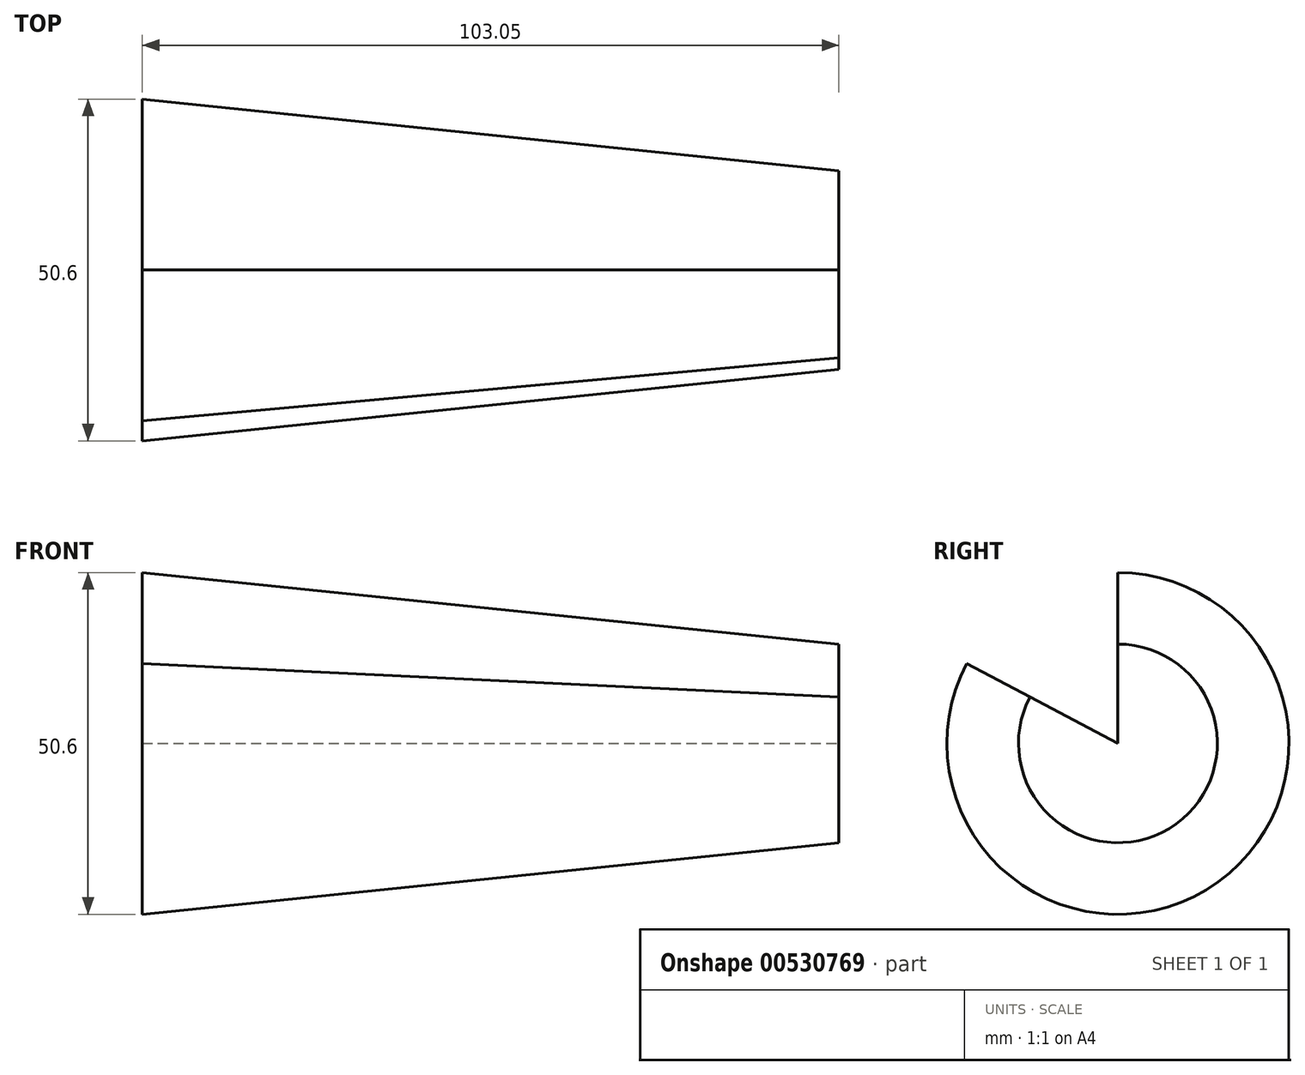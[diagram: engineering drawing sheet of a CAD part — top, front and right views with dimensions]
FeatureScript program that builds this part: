
annotation { "Feature Type Name" : "Feature", "Feature Type Description" : "" }
export const myFeature = defineFeature(function(context is Context, id is Id, definition is map)
    precondition{}
    {
        {
            var Q0;
            Q0=qCreatedBy(makeId("Front.planeOp"),FACE);
            var sketch = newSketch(context, id + "F0", { "sketchPlane" : qUnion([Q0])});
            skLineSegment(sketch, "E0.bottom", {"start": v(0, 0) * mm, "end": v(103.05, 0) * mm});
            skLineSegment(sketch, "E0.left", {"start": v(0, 0) * mm, "end": v(0, 25.3) * mm});
            skLineSegment(sketch, "E0.right", {"start": v(103.05, 0) * mm, "end": v(103.05, 14.7) * mm});
            skLineSegment(sketch, "E1", {"start": v(-48.8, 0) * mm, "end": v(81.05, 0) * mm, "construction": true});
            skLineSegment(sketch, "E2", {"start": v(103.05, 14.7) * mm, "end": v(0, 25.3) * mm});
            skSolve(sketch);
        }
        {
            var Q0;
            Q0=makeQuery(id+"F0.imprint","IMPRINT",FACE,{"disambiguationData":[TD([[makeQuery(id+"F0.imprint","IMPRINT",EDGE,{"derivedFrom":sQuery(id+"F0.wireOp",EDGE,"E0.bottom")}),1.0]])]});
            var Q1;
            Q1=sQuery(id+"F0.wireOp",EDGE,"E1");
            revolve(context, id + "F1", {"entities" : qUnion([Q0]), "axis" : qUnion([Q1]), "revolveType" : RevolveType.ONE_DIRECTION, "oppositeDirection" : true, "angle" : 297.9 * degree});
        }
    });
